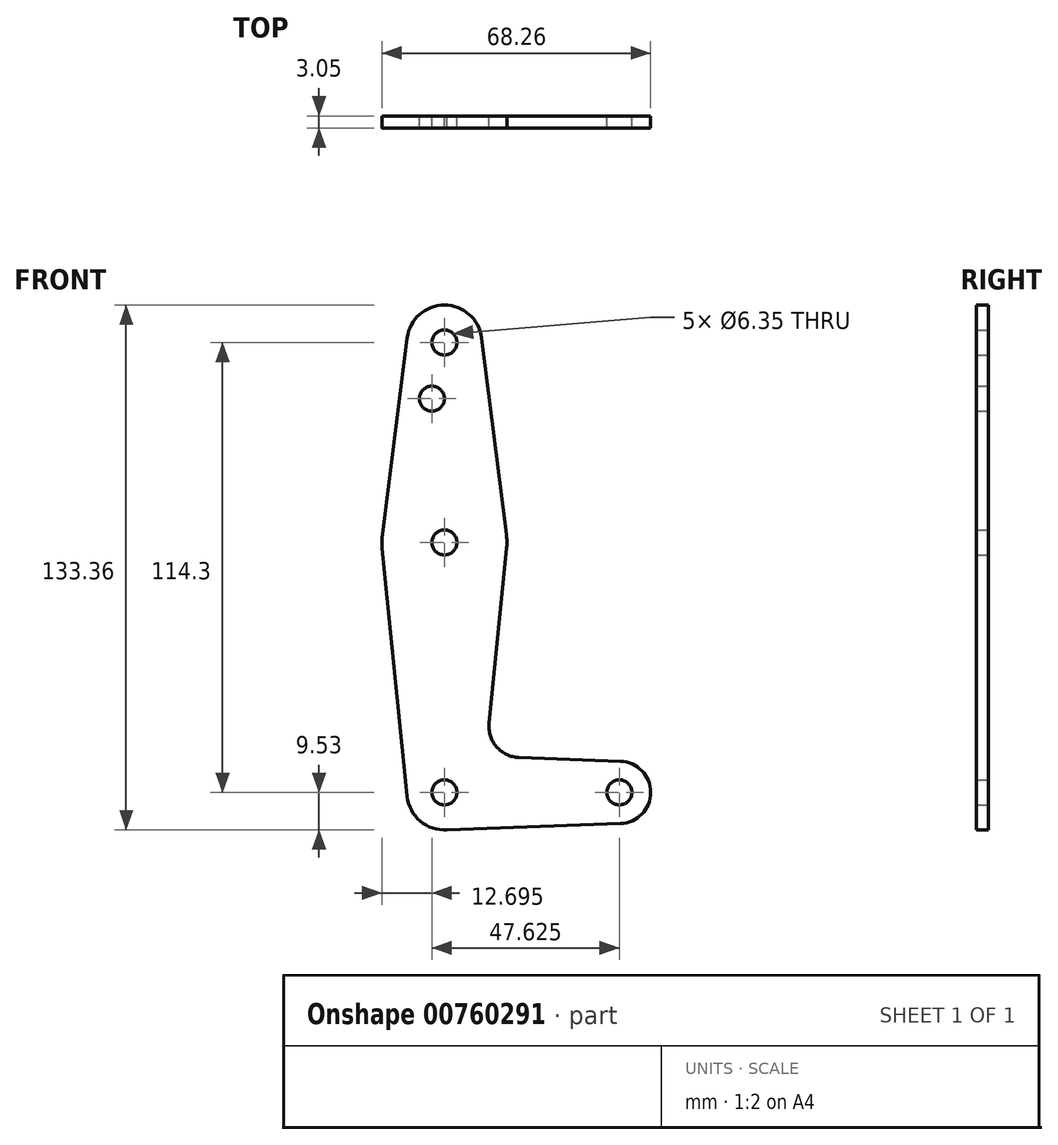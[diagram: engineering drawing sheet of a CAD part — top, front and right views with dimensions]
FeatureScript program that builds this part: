
annotation { "Feature Type Name" : "Feature", "Feature Type Description" : "" }
export const myFeature = defineFeature(function(context is Context, id is Id, definition is map)
    precondition{}
    {
        {
            var Q0;
            Q0=qCreatedBy(makeId("Front.planeOp"),FACE);
            var sketch = newSketch(context, id + "F0", { "sketchPlane" : qUnion([Q0])});
            skCircle(sketch, "E0", {"center": v(0, 0) * mm, "radius": 9.53 * mm});
            skCircle(sketch, "E1", {"center": v(0, 63.5) * mm, "radius": 15.88 * mm});
            skCircle(sketch, "E2", {"center": v(0, 114.3) * mm, "radius": 9.52 * mm});
            skCircle(sketch, "E3", {"center": v(44.45, 0) * mm, "radius": 7.94 * mm});
            skLineSegment(sketch, "E4", {"start": v(44.45, 0) * mm, "end": v(0, 0) * mm, "construction": true});
            skLineSegment(sketch, "E5", {"start": v(0, 114.3) * mm, "end": v(0, 0) * mm, "construction": true});
            skLineSegment(sketch, "E6", {"start": v(-15.75, 65.48) * mm, "end": v(-9.45, 115.5) * mm});
            skLineSegment(sketch, "E7", {"start": v(9.45, 115.5) * mm, "end": v(15.75, 65.48) * mm});
            skLineSegment(sketch, "E8", {"start": v(18.97, 8.85) * mm, "end": v(44.73, 7.93) * mm});
            skLineSegment(sketch, "E9", {"start": v(0, -9.53) * mm, "end": v(44.73, -7.93) * mm});
            skLineSegment(sketch, "E10", {"start": v(15.8, 61.91) * mm, "end": v(11.34, 17.6) * mm});
            skLineSegment(sketch, "E11", {"start": v(-15.8, 61.91) * mm, "end": v(-9.48, -0.95) * mm});
            skCircle(sketch, "E12", {"center": v(0, 114.3) * mm, "radius": 3.18 * mm});
            skCircle(sketch, "E13", {"center": v(0, 63.5) * mm, "radius": 3.18 * mm});
            skCircle(sketch, "E14", {"center": v(0, 0) * mm, "radius": 3.18 * mm});
            skCircle(sketch, "E15", {"center": v(44.45, 0) * mm, "radius": 3.18 * mm});
            skCircle(sketch, "E16", {"center": v(-3.17, 100.03) * mm, "radius": 3.18 * mm});
            skArc(sketch, "E17.filletArc", {"start": v(11.34, 17.6) * mm, "mid": v(13.26, 11.57) * mm, "end": v(18.97, 8.85) * mm});
            skSolve(sketch);
        }
        {
            var Q0;
            Q0 = qSketchRegion(id + "F0", true);
            extrude(context, id + "F1", {"entities" : qUnion([Q0]), "depth" : 3.05 * mm, "offsetDistance" : 25.4 * mm});
        }
    });
